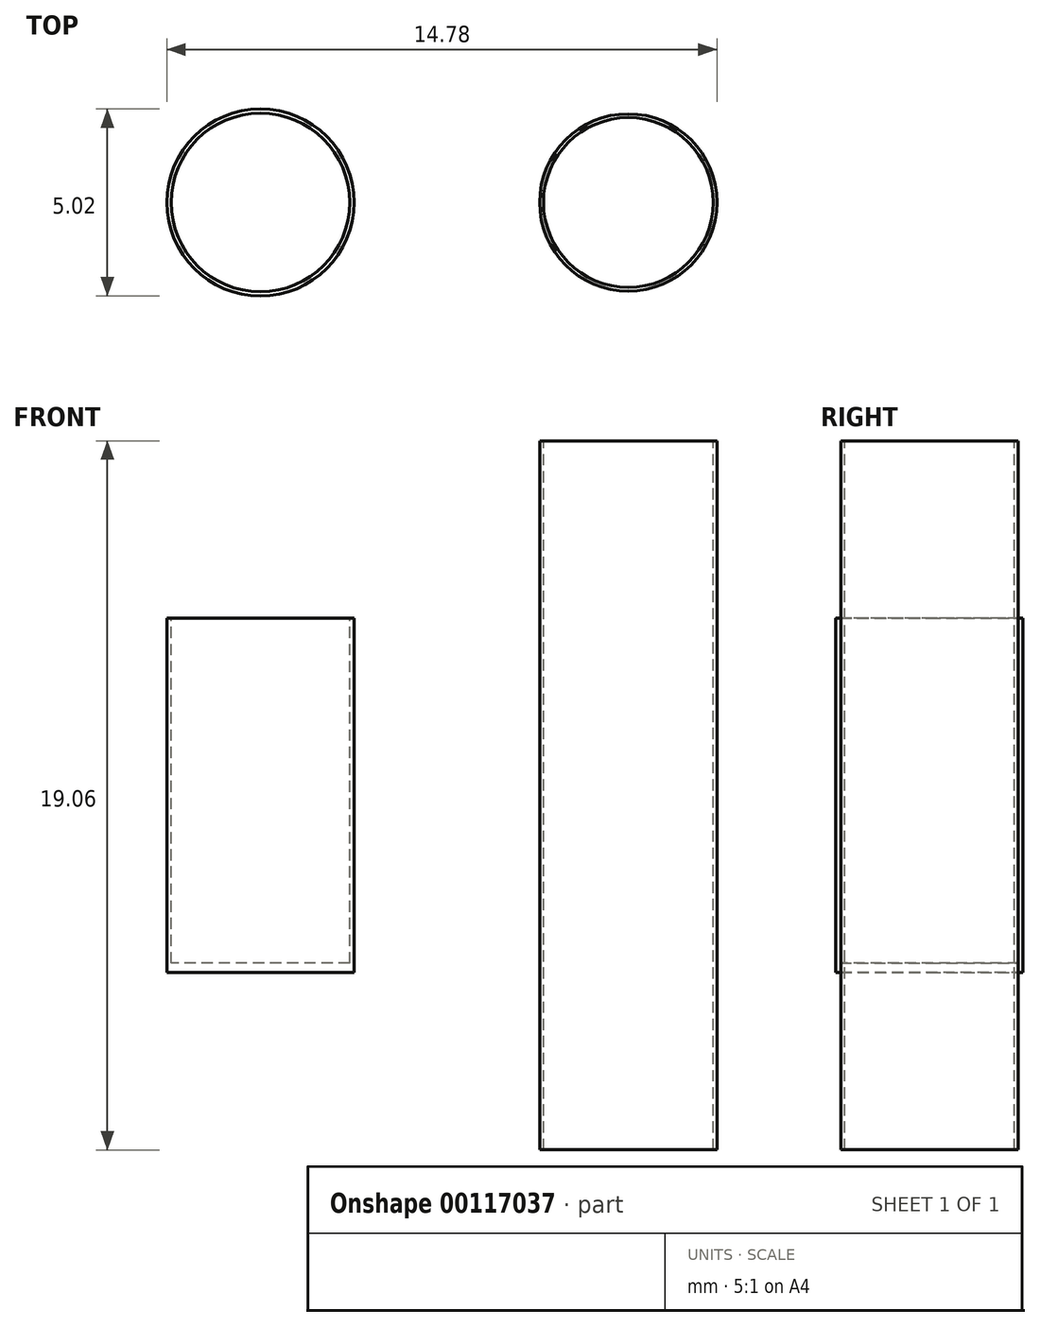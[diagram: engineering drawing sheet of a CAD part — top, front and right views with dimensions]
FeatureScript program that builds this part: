
annotation { "Feature Type Name" : "Feature", "Feature Type Description" : "" }
export const myFeature = defineFeature(function(context is Context, id is Id, definition is map)
    precondition{}
    {
        {
            var Q0;
            Q0=qCreatedBy(makeId("Top.planeOp"),FACE);
            var sketch = newSketch(context, id + "F0", { "sketchPlane" : qUnion([Q0])});
            skCircle(sketch, "E0", {"center": v(0, 0) * mm, "radius": 2.38 * mm});
            skCircle(sketch, "E1", {"center": v(-9.89, 0) * mm, "radius": 2.51 * mm});
            skSolve(sketch);
        }
        {
            var Q0;
            Q0=makeQuery(id+"F0.imprint","IMPRINT",FACE,{"disambiguationData":[TD([[makeQuery(id+"F0.imprint","IMPRINT",EDGE,{"derivedFrom":sQuery(id+"F0.wireOp",EDGE,"E0")}),1.0]])]});
            extrude(context, id + "F1", {"entities" : qUnion([Q0]), "endBound" : BoundingType.SYMMETRIC, "depth" : 19.05 * mm});
        }
        {
            var Q0;
            Q0=makeQuery(id+"F1.opExtrude","CAP_FACE",FACE,{"disambiguationData":[OSD([sQuery(id+"F0.wireOp",EDGE,"E0")])],"isStart":false});
            var sketch = newSketch(context, id + "F2", { "sketchPlane" : qUnion([Q0])});
            skCircle(sketch, "E2", {"center": v(0, 0) * mm, "radius": 2.28 * mm});
            skSolve(sketch);
        }
        {
            var Q0;
            Q0=makeQuery(id+"F2.imprint","IMPRINT",FACE,{"disambiguationData":[TD([[makeQuery(id+"F2.imprint","IMPRINT",EDGE,{"derivedFrom":sQuery(id+"F2.wireOp",EDGE,"E2")}),1.0]])]});
            extrude(context, id + "F3", {"entities" : qUnion([Q0]), "operationType" : NewBodyOperationType.REMOVE, "oppositeDirection" : true, "depth" : 19.05 * mm});
        }
        {
            var Q0;
            Q0=makeQuery(id+"F0.imprint","IMPRINT",FACE,{"disambiguationData":[TD([[makeQuery(id+"F0.imprint","IMPRINT",EDGE,{"derivedFrom":sQuery(id+"F0.wireOp",EDGE,"E1")}),1.0]])]});
            extrude(context, id + "F4", {"entities" : qUnion([Q0]), "endBound" : BoundingType.SYMMETRIC, "depth" : 9.52 * mm});
        }
        {
            var Q0;
            Q0=makeQuery(id+"F4.opExtrude","CAP_FACE",FACE,{"disambiguationData":[OSD([sQuery(id+"F0.wireOp",EDGE,"E1")])],"isStart":false});
            var sketch = newSketch(context, id + "F5", { "sketchPlane" : qUnion([Q0])});
            skCircle(sketch, "E3", {"center": v(-9.89, 0) * mm, "radius": 2.4 * mm});
            skSolve(sketch);
        }
        {
            var Q0;
            Q0=makeQuery(id+"F5.imprint","IMPRINT",FACE,{"disambiguationData":[TD([[makeQuery(id+"F5.imprint","IMPRINT",EDGE,{"derivedFrom":sQuery(id+"F5.wireOp",EDGE,"E3")}),1.0]])]});
            extrude(context, id + "F6", {"entities" : qUnion([Q0]), "operationType" : NewBodyOperationType.REMOVE, "oppositeDirection" : true, "depth" : 9.27 * mm});
        }
    });
